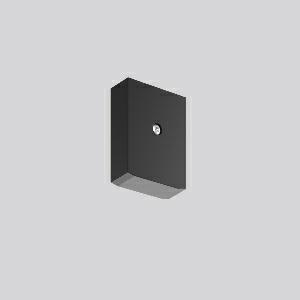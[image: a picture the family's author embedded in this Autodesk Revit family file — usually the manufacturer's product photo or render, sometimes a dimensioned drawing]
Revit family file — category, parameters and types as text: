
# Revit family: linedo_endkappe_b_f_982700_003_e18c
name_source: partatom
category: Lighting Fixtures
units: mm (PartAtom-declared; Revit-internal decimal feet)

## family parameters
Cut with Voids When Loaded = No
Host = Face
Light Source = No
Part Type = Normal
Room Calculation Point = No
Round Connector Dimension = Use Diameter
Shared = No

## types (1)
- LINEDO_Endkappe_B_F
    Apparent Load = 0 VA
    Default Elevation = 1800 mm
    Description = End cap low profile for LINEDO plug. Plastic end cap to cover the LINEDO plug system at the end of the line. Fastening by TX20 screw. Installation accessories included.
Colour: black
Length: 23 mm
Width: 58 mm
Height: 76 mm
Weight: 31 g
    Height = 76 mm
    Lamp = 0 x
    Length = 23 mm
    Luminous efficacy = 0 lm/W
    Manufacturer = RZB
    ModVariant = No
    Model = 982700.003
    Mounting Place = Ceiling
    Mounting Type = Surface mounted, Pendant
    Number of Poles = 1
    OnlyDefault = Yes
    Power Factor = 1
    Product Name = LINEDO_Endkappe_B_F
    Product group = Surface mounted continuous line luminaire system
    ProductGroupID = 310
    Protection Class = Protection class
    Protection Degree = Degree of protection
    RLX_Detail_Level = 1
    RLX_Emergency_Light_Flux = 0 lm
    RLX_Emergency_Type = 0
    RLX_Emergency_Type_DB = No
    RlxData = <blob elided: 10413 chars, md5=67011523>
    Standby Power = 0 W
    System Light Flux = 0 lm
    System Power = 0 W
    Type Comments = Product without accessories
    Type Image = 982700.003.jpg
    URL = http://relux.com
    VarID = ---
    Voltage = 0 V
    Weight = 0.00 kg
    Width = 58 mm

## geometry (parser evidence)
native form markers: Sweep x8
no freeform markers — native parametric forms only
